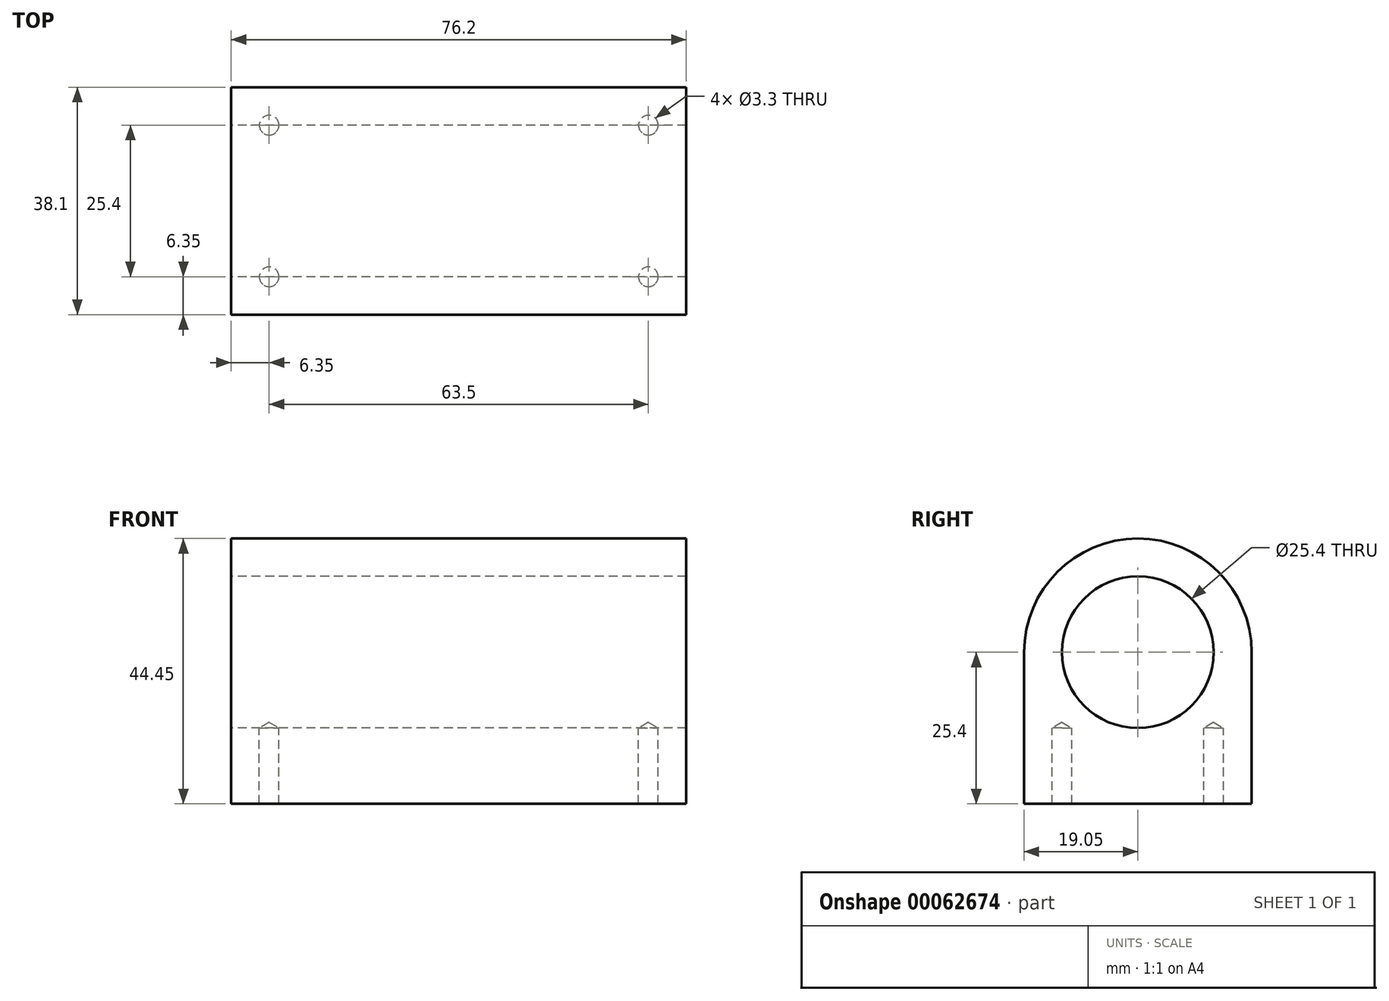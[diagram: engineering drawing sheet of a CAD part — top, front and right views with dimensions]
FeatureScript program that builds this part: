
annotation { "Feature Type Name" : "Feature", "Feature Type Description" : "" }
export const myFeature = defineFeature(function(context is Context, id is Id, definition is map)
    precondition{}
    {
        {
            var Q0;
            Q0=qCreatedBy(makeId("Right.planeOp"),FACE);
            var sketch = newSketch(context, id + "F0", { "sketchPlane" : qUnion([Q0])});
            skLineSegment(sketch, "E0.bottom", {"start": v(-12.7, 0) * mm, "end": v(12.7, 0) * mm});
            skLineSegment(sketch, "E0.top", {"start": v(-19.05, -25.4) * mm, "end": v(19.05, -25.4) * mm});
            skLineSegment(sketch, "E0.left", {"start": v(-19.05, 0) * mm, "end": v(-19.05, -25.4) * mm});
            skLineSegment(sketch, "E0.right", {"start": v(19.05, 0) * mm, "end": v(19.05, -25.4) * mm});
            skArc(sketch, "E1", {"start": v(19.05, 0) * mm, "mid": v(0, 19.05) * mm, "end": v(-19.05, 0) * mm});
            skCircle(sketch, "E2", {"center": v(0, 0) * mm, "radius": 12.7 * mm});
            skLineSegment(sketch, "E3.trimOffspring", {"start": v(19.05, 0) * mm, "end": v(19.05, 0) * mm});
            skSolve(sketch);
        }
        {
            var Q0;
            Q0=makeQuery(id+"F0.imprint","IMPRINT",FACE,{"disambiguationData":[TD([[makeQuery(id+"F0.imprint","IMPRINT",EDGE,{"derivedFrom":sQuery(id+"F0.wireOp",EDGE,"E0.top")}),1.0]])]});
            extrude(context, id + "F1", {"entities" : qUnion([Q0]), "depth" : 76.2 * mm});
        }
        {
            var Q0;
            Q0=makeQuery(id+"F1.opExtrude","SWEPT_FACE",FACE,{"disambiguationData":[OSD([sQuery(id+"F0.wireOp",EDGE,"E0.top")])]});
            var sketch = newSketch(context, id + "F2", { "sketchPlane" : qUnion([Q0])});
            skCircle(sketch, "E4", {"center": v(6.35, 12.7) * mm, "radius": 1.65 * mm});
            skCircle(sketch, "E5", {"center": v(69.85, 12.7) * mm, "radius": 1.65 * mm});
            skCircle(sketch, "E6", {"center": v(69.85, -12.7) * mm, "radius": 1.65 * mm});
            skCircle(sketch, "E7", {"center": v(6.35, -12.7) * mm, "radius": 1.65 * mm});
            skSolve(sketch);
        }
        {
            var Q0;
            Q0=sQuery(id+"F2.wireOp",VERTEX,"E4.center");
            var Q1;
            Q1=sQuery(id+"F2.wireOp",VERTEX,"E7.center");
            var Q2;
            Q2=sQuery(id+"F2.wireOp",VERTEX,"E6.center");
            var Q3;
            Q3=sQuery(id+"F2.wireOp",VERTEX,"E5.center");
            var Q4;
            Q4=makeQuery(id+"F1.opExtrude","SWEPT_BODY",BODY,{"disambiguationData":[OSD([sQuery(id+"F0.wireOp",EDGE,"E0.top"),sQuery(id+"F0.wireOp",EDGE,"E0.left"),sQuery(id+"F0.wireOp",EDGE,"E0.right"),sQuery(id+"F0.wireOp",EDGE,"E1"),sQuery(id+"F0.wireOp",EDGE,"E2")])]});
            hole(context, id + "F3", {"style" : HoleStyle.SIMPLE, "holeDiameter" : 3.3 * mm, "endStyle" : HoleEndStyle.BLIND, "holeDepth" : 12.7 * mm, "locations" : qUnion([Q0, Q1, Q2, Q3]), "scope" : qUnion([Q4])});
        }
    });
